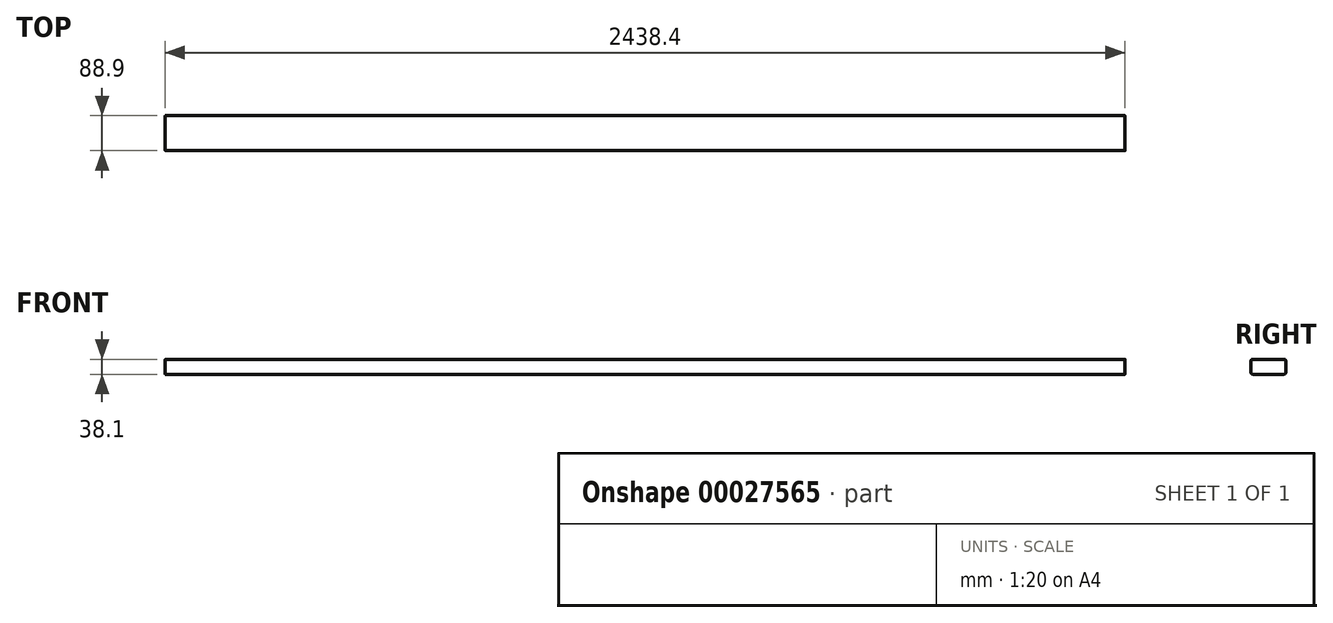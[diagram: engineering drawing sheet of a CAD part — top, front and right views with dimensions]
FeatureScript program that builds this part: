
annotation { "Feature Type Name" : "Feature", "Feature Type Description" : "" }
export const myFeature = defineFeature(function(context is Context, id is Id, definition is map)
    precondition{}
    {
        {
            var Q0;
            Q0=qCreatedBy(makeId("Right.planeOp"),FACE);
            var sketch = newSketch(context, id + "F0", { "sketchPlane" : qUnion([Q0])});
            skLineSegment(sketch, "E0.bottom", {"start": v(0, 0) * mm, "end": v(88.9, 0) * mm});
            skLineSegment(sketch, "E0.top", {"start": v(0, 38.1) * mm, "end": v(88.9, 38.1) * mm});
            skLineSegment(sketch, "E0.left", {"start": v(0, 0) * mm, "end": v(0, 38.1) * mm});
            skLineSegment(sketch, "E0.right", {"start": v(88.9, 0) * mm, "end": v(88.9, 38.1) * mm});
            skSolve(sketch);
        }
        {
            var Q0;
            Q0 = qSketchRegion(id + "F0", true);
            extrude(context, id + "F1", {"entities" : qUnion([Q0]), "depth" : 2438.4 * mm});
        }
        {
            var Q0;
            Q0=makeQuery(id+"F1.opExtrude","SWEPT_EDGE",EDGE,{"disambiguationData":[OSD([sQuery(id+"F0.wireOp",EDGE,"E0.top"),sQuery(id+"F0.wireOp",EDGE,"E0.left")])]});
            var Q1;
            Q1=makeQuery(id+"F1.opExtrude","SWEPT_EDGE",EDGE,{"disambiguationData":[OSD([sQuery(id+"F0.wireOp",EDGE,"E0.bottom"),sQuery(id+"F0.wireOp",EDGE,"E0.left")])]});
            var Q2;
            Q2=makeQuery(id+"F1.opExtrude","SWEPT_EDGE",EDGE,{"disambiguationData":[OSD([sQuery(id+"F0.wireOp",EDGE,"E0.top"),sQuery(id+"F0.wireOp",EDGE,"E0.right")])]});
            fillet(context, id + "F2", {"entities" : qUnion([Q0, Q1, Q2]), "radius" : 5.08 * mm, "tangentPropagation" : true, "allowEdgeOverflow" : false});
        }
        {
            var Q0;
            Q0=makeQuery(id+"F1.opExtrude","SWEPT_EDGE",EDGE,{"disambiguationData":[OSD([sQuery(id+"F0.wireOp",EDGE,"E0.bottom"),sQuery(id+"F0.wireOp",EDGE,"E0.right")])]});
            fillet(context, id + "F3", {"entities" : qUnion([Q0]), "radius" : 5.08 * mm, "tangentPropagation" : true, "allowEdgeOverflow" : false});
        }
    });
